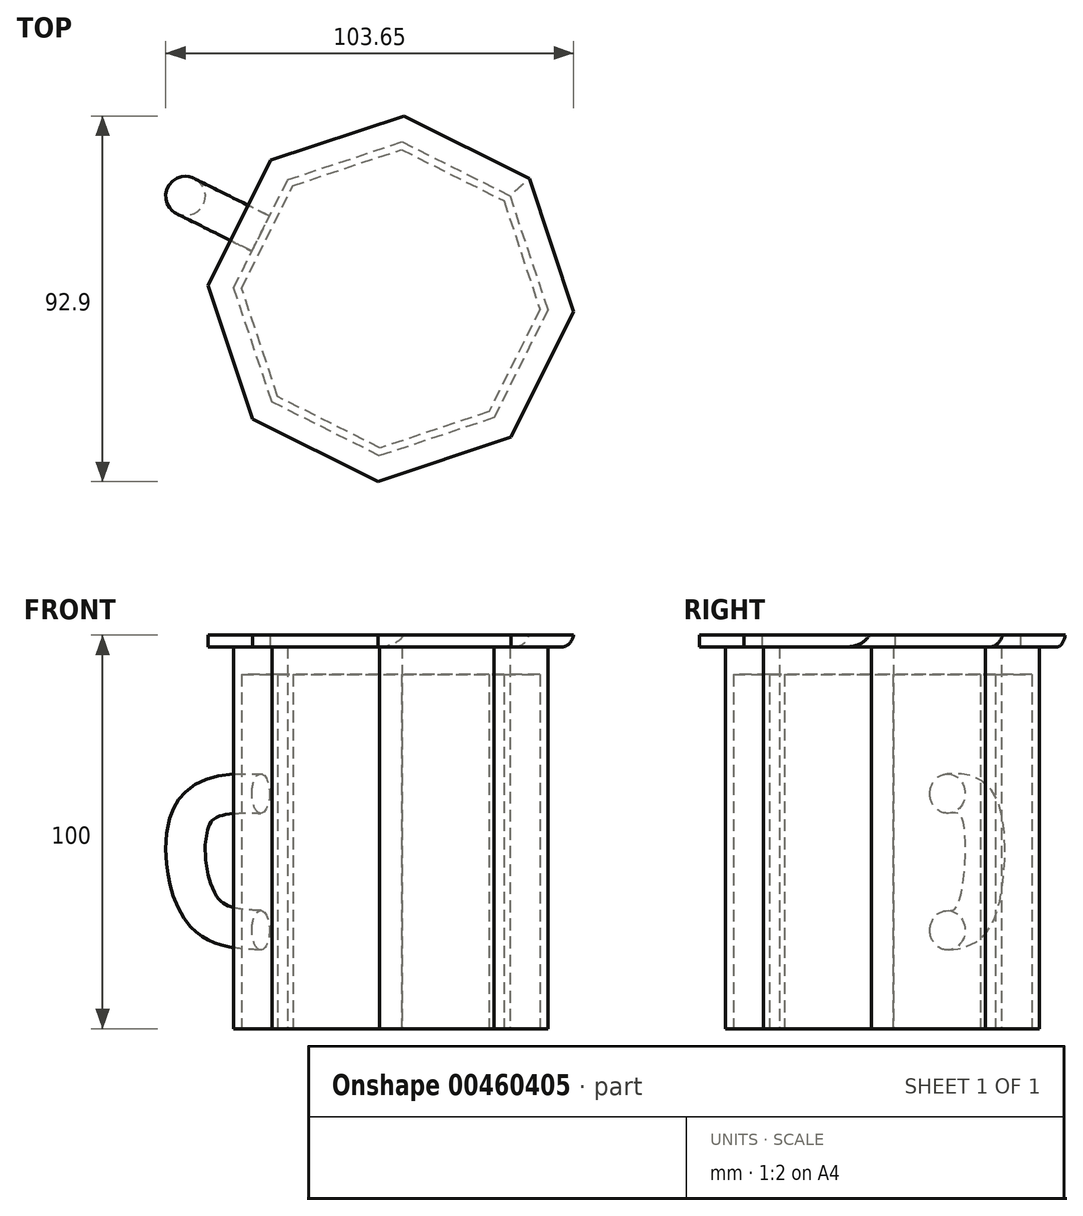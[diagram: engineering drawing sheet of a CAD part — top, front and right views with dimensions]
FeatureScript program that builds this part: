
annotation { "Feature Type Name" : "Feature", "Feature Type Description" : "" }
export const myFeature = defineFeature(function(context is Context, id is Id, definition is map)
    precondition{}
    {
        {
            var Q0;
            Q0=qCreatedBy(makeId("Top.planeOp"),FACE);
            var sketch = newSketch(context, id + "F0", { "sketchPlane" : qUnion([Q0])});
            skCircle(sketch, "E0.cCircle", {"center": v(0, 0) * mm, "radius": 36.96 * mm, "construction": true});
            skLineSegment(sketch, "E0.0", {"start": v(39.9, -2.84) * mm, "end": v(26.2, -30.22) * mm});
            skLineSegment(sketch, "E0.1", {"start": v(26.2, -30.22) * mm, "end": v(-2.84, -39.9) * mm});
            skLineSegment(sketch, "E0.2", {"start": v(-2.84, -39.9) * mm, "end": v(-30.22, -26.2) * mm});
            skLineSegment(sketch, "E0.3", {"start": v(-30.22, -26.2) * mm, "end": v(-39.9, 2.84) * mm});
            skLineSegment(sketch, "E0.4", {"start": v(-39.9, 2.84) * mm, "end": v(-26.2, 30.22) * mm});
            skLineSegment(sketch, "E0.5", {"start": v(-26.2, 30.22) * mm, "end": v(2.84, 39.9) * mm});
            skLineSegment(sketch, "E0.6", {"start": v(2.84, 39.9) * mm, "end": v(30.22, 26.2) * mm});
            skLineSegment(sketch, "E0.7", {"start": v(30.22, 26.2) * mm, "end": v(39.9, -2.84) * mm});
            skPoint(sketch, "E0.0.midPoint", {"position": v(33.05, -16.53) * mm});
            skCircle(sketch, "E1.cCircle", {"center": v(0, 0) * mm, "radius": 35.1 * mm, "construction": true});
            skLineSegment(sketch, "E1.0", {"start": v(-24.9, 28.71) * mm, "end": v(2.7, 37.9) * mm});
            skLineSegment(sketch, "E1.1", {"start": v(2.7, 37.9) * mm, "end": v(28.71, 24.9) * mm});
            skLineSegment(sketch, "E1.2", {"start": v(28.71, 24.9) * mm, "end": v(37.9, -2.7) * mm});
            skLineSegment(sketch, "E1.3", {"start": v(37.9, -2.7) * mm, "end": v(24.9, -28.71) * mm});
            skLineSegment(sketch, "E1.4", {"start": v(24.9, -28.71) * mm, "end": v(-2.7, -37.9) * mm});
            skLineSegment(sketch, "E1.5", {"start": v(-2.7, -37.9) * mm, "end": v(-28.71, -24.9) * mm});
            skLineSegment(sketch, "E1.6", {"start": v(-28.71, -24.9) * mm, "end": v(-37.9, 2.7) * mm});
            skLineSegment(sketch, "E1.7", {"start": v(-37.9, 2.7) * mm, "end": v(-24.9, 28.71) * mm});
            skPoint(sketch, "E1.0.midPoint", {"position": v(-11.1, 33.3) * mm});
            skLineSegment(sketch, "E2", {"start": v(2.84, 39.9) * mm, "end": v(0, 0) * mm, "construction": true});
            skSolve(sketch);
        }
        {
            var Q0;
            Q0=makeQuery(id+"F0.imprint","IMPRINT",FACE,{"disambiguationData":[TD([[makeQuery(id+"F0.imprint","IMPRINT",EDGE,{"derivedFrom":sQuery(id+"F0.wireOp",EDGE,"E1.0")}),-1.0]])]});
            var Q1;
            Q1=makeQuery(id+"F0.imprint","IMPRINT",FACE,{"disambiguationData":[TD([[makeQuery(id+"F0.imprint","IMPRINT",EDGE,{"derivedFrom":sQuery(id+"F0.wireOp",EDGE,"E0.0")}),-1.0]])]});
            extrude(context, id + "F1", {"entities" : qUnion([Q0, Q1]), "depth" : 100 * mm});
        }
        {
            var Q0;
            Q0=makeQuery(id+"F0.imprint","IMPRINT",FACE,{"disambiguationData":[TD([[makeQuery(id+"F0.imprint","IMPRINT",EDGE,{"derivedFrom":sQuery(id+"F0.wireOp",EDGE,"E1.0")}),-1.0]])]});
            extrude(context, id + "F2", {"entities" : qUnion([Q0]), "operationType" : NewBodyOperationType.REMOVE, "depth" : 90 * mm});
        }
        {
            var Q0;
            Q0=makeQuery(id+"F1.opExtrude","SWEPT_FACE",FACE,{"disambiguationData":[OSD([sQuery(id+"F0.wireOp",EDGE,"E0.2")])]});
            cPlane(context, id + "F3", {"entities" : qUnion([Q0]), "cplaneType" : CPlaneType.OFFSET, "offset" : 36.95 * mm, "oppositeDirection" : true, "width" : 150 * mm, "height" : 150 * mm});
        }
        {
            var Q0;
            Q0=makeQuery(id+"F1.opExtrude","SWEPT_FACE",FACE,{"disambiguationData":[OSD([sQuery(id+"F0.wireOp",EDGE,"E0.4")])]});
            var sketch = newSketch(context, id + "F4", { "sketchPlane" : qUnion([Q0])});
            skCircle(sketch, "E3", {"center": v(0, 25) * mm, "radius": 5 * mm});
            skSolve(sketch);
        }
        {
            var Q0;
            Q0=qCreatedBy(id+"F3.planeOp",FACE);
            var sketch = newSketch(context, id + "F5", { "sketchPlane" : qUnion([Q0])});
            skFitSpline(sketch, "E4", {"points": [v(-36.89, 24.92) * mm, v(-53.96, 30.53) * mm, v(-56.17, 54.83) * mm, v(-36.84, 59.8) * mm], "startDerivative": vector(-62.83, 2.5) * mm, "endDerivative": vector(72.33, -1.46) * mm});
            skSolve(sketch);
        }
        {
            var Q0;
            Q0=makeQuery(id+"F4.imprint","IMPRINT",FACE,{"disambiguationData":[TD([[makeQuery(id+"F4.imprint","IMPRINT",EDGE,{"derivedFrom":sQuery(id+"F4.wireOp",EDGE,"E3")}),1.0]])]});
            var Q1;
            Q1=sQuery(id+"F5.wireOp",EDGE,"E4");
            sweep(context, id + "F6", {"operationType" : NewBodyOperationType.ADD, "profiles" : qUnion([Q0]), "path" : qUnion([Q1])});
        }
        {
            var Q0;
            Q0=makeQuery(id+"F1.opExtrude","CAP_FACE",FACE,{"disambiguationData":[OSD([sQuery(id+"F0.wireOp",EDGE,"E0.0"),sQuery(id+"F0.wireOp",EDGE,"E0.1"),sQuery(id+"F0.wireOp",EDGE,"E0.2"),sQuery(id+"F0.wireOp",EDGE,"E0.3"),sQuery(id+"F0.wireOp",EDGE,"E0.4"),sQuery(id+"F0.wireOp",EDGE,"E0.5"),sQuery(id+"F0.wireOp",EDGE,"E0.6"),sQuery(id+"F0.wireOp",EDGE,"E0.7")])],"isStart":false});
            fillet(context, id + "F7", {"entities" : qUnion([Q0]), "radius" : 1.93 * mm, "tangentPropagation" : true, "allowEdgeOverflow" : false});
        }
        {
            var Q0;
            Q0=makeQuery(id+"F1.opExtrude","CAP_FACE",FACE,{"disambiguationData":[OSD([sQuery(id+"F0.wireOp",EDGE,"E0.0"),sQuery(id+"F0.wireOp",EDGE,"E0.1"),sQuery(id+"F0.wireOp",EDGE,"E0.2"),sQuery(id+"F0.wireOp",EDGE,"E0.3"),sQuery(id+"F0.wireOp",EDGE,"E0.4"),sQuery(id+"F0.wireOp",EDGE,"E0.5"),sQuery(id+"F0.wireOp",EDGE,"E0.6"),sQuery(id+"F0.wireOp",EDGE,"E0.7")])],"isStart":false});
            var sketch = newSketch(context, id + "F8", { "sketchPlane" : qUnion([Q0])});
            skLineSegment(sketch, "E5.0", {"start": v(-3.3, -46.45) * mm, "end": v(30.51, -35.18) * mm});
            skLineSegment(sketch, "E5.1", {"start": v(-35.18, -30.51) * mm, "end": v(-3.3, -46.45) * mm});
            skLineSegment(sketch, "E5.2", {"start": v(30.51, -35.18) * mm, "end": v(46.45, -3.3) * mm});
            skLineSegment(sketch, "E5.3", {"start": v(-46.45, 3.3) * mm, "end": v(-35.18, -30.51) * mm});
            skLineSegment(sketch, "E5.4", {"start": v(46.45, -3.3) * mm, "end": v(35.18, 30.51) * mm});
            skLineSegment(sketch, "E5.5", {"start": v(35.18, 30.51) * mm, "end": v(3.3, 46.45) * mm});
            skLineSegment(sketch, "E5.6", {"start": v(3.3, 46.45) * mm, "end": v(-30.51, 35.18) * mm});
            skLineSegment(sketch, "E5.7", {"start": v(-30.51, 35.18) * mm, "end": v(-46.45, 3.3) * mm});
            skSolve(sketch);
        }
        {
            var Q0;
            Q0 = qSketchRegion(id + "F8", true);
            extrude(context, id + "F9", {"entities" : qUnion([Q0]), "operationType" : NewBodyOperationType.ADD, "oppositeDirection" : true, "depth" : 3 * mm});
        }
        {
            var Q0;
            Q0=makeQuery(id+"F9.opExtrude","CAP_EDGE",EDGE,{"disambiguationData":[OSD([sQuery(id+"F8.wireOp",EDGE,"E5.4")])],"isStart":false});
            var Q1;
            Q1=makeQuery(id+"F9.opExtrude","CAP_EDGE",EDGE,{"disambiguationData":[OSD([sQuery(id+"F8.wireOp",EDGE,"E5.5")])],"isStart":false});
            fillet(context, id + "F10", {"entities" : qUnion([Q0, Q1]), "radius" : 5 * mm, "tangentPropagation" : true, "allowEdgeOverflow" : false});
        }
    });
